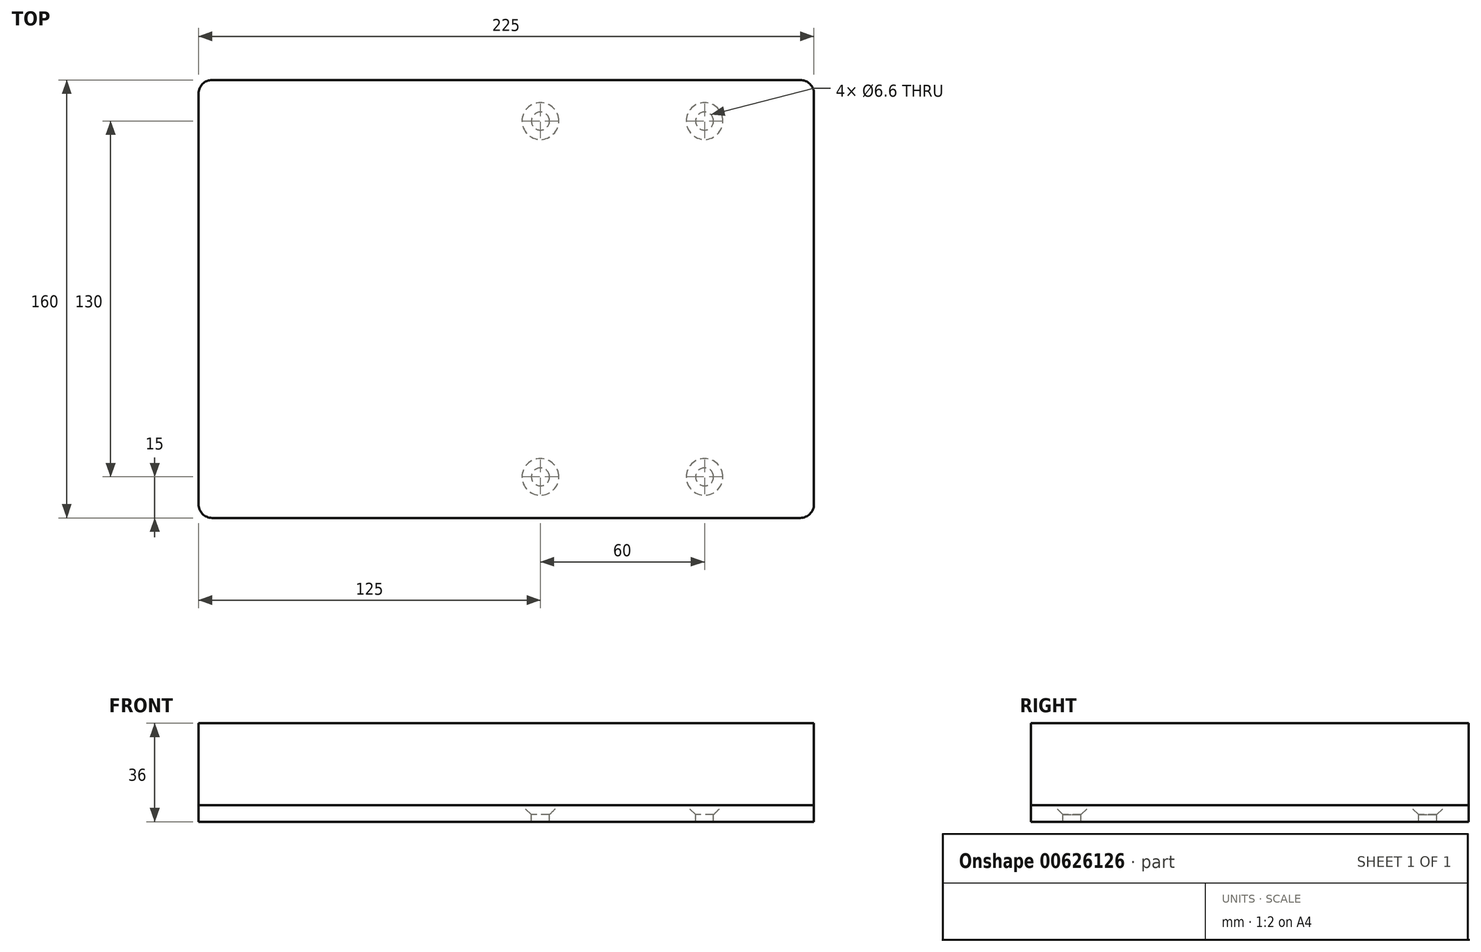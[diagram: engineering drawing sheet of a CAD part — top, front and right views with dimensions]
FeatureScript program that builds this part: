
annotation { "Feature Type Name" : "Feature", "Feature Type Description" : "" }
export const myFeature = defineFeature(function(context is Context, id is Id, definition is map)
    precondition{}
    {
        {
            var Q0;
            Q0=qCreatedBy(makeId("Top.planeOp"),FACE);
            var sketch = newSketch(context, id + "F0", { "sketchPlane" : qUnion([Q0])});
            skLineSegment(sketch, "E0.bottom", {"start": v(112.5, -80) * mm, "end": v(-112.5, -80) * mm});
            skLineSegment(sketch, "E0.top", {"start": v(112.5, 80) * mm, "end": v(-112.5, 80) * mm});
            skLineSegment(sketch, "E0.left", {"start": v(112.5, -80) * mm, "end": v(112.5, 80) * mm});
            skLineSegment(sketch, "E0.right", {"start": v(-112.5, -80) * mm, "end": v(-112.5, 80) * mm});
            skPoint(sketch, "E0.middle", {"position": v(0, 0) * mm});
            skSolve(sketch);
        }
        {
            var Q0;
            Q0=makeQuery(id+"F0.imprint","IMPRINT",FACE,{"disambiguationData":[TD([[makeQuery(id+"F0.imprint","IMPRINT",EDGE,{"derivedFrom":sQuery(id+"F0.wireOp",EDGE,"E0.bottom")}),-1.0]])]});
            extrude(context, id + "F1", {"entities" : qUnion([Q0]), "depth" : 6 * mm, "offsetDistance" : 25 * mm});
        }
        {
            var Q0;
            Q0=makeQuery(id+"F1.opExtrude","SWEPT_EDGE",EDGE,{"disambiguationData":[OSD([sQuery(id+"F0.wireOp",EDGE,"E0.bottom"),sQuery(id+"F0.wireOp",EDGE,"E0.left")])]});
            var Q1;
            Q1=makeQuery(id+"F1.opExtrude","SWEPT_EDGE",EDGE,{"disambiguationData":[OSD([sQuery(id+"F0.wireOp",EDGE,"E0.top"),sQuery(id+"F0.wireOp",EDGE,"E0.left")])]});
            var Q2;
            Q2=makeQuery(id+"F1.opExtrude","SWEPT_EDGE",EDGE,{"disambiguationData":[OSD([sQuery(id+"F0.wireOp",EDGE,"E0.bottom"),sQuery(id+"F0.wireOp",EDGE,"E0.right")])]});
            var Q3;
            Q3=makeQuery(id+"F1.opExtrude","SWEPT_EDGE",EDGE,{"disambiguationData":[OSD([sQuery(id+"F0.wireOp",EDGE,"E0.top"),sQuery(id+"F0.wireOp",EDGE,"E0.right")])]});
            fillet(context, id + "F2", {"entities" : qUnion([Q0, Q1, Q2, Q3]), "radius" : 5 * mm, "tangentPropagation" : true, "allowEdgeOverflow" : false});
        }
        {
            var Q0;
            Q0=makeQuery(id+"F1.opExtrude","CAP_FACE",FACE,{"disambiguationData":[OSD([sQuery(id+"F0.wireOp",EDGE,"E0.bottom"),sQuery(id+"F0.wireOp",EDGE,"E0.top"),sQuery(id+"F0.wireOp",EDGE,"E0.left"),sQuery(id+"F0.wireOp",EDGE,"E0.right")])],"isStart":false});
            var sketch = newSketch(context, id + "F3", { "sketchPlane" : qUnion([Q0])});
            skLineSegment(sketch, "E1", {"start": v(-230.2, 65) * mm, "end": v(230.97, 65) * mm, "construction": true});
            skLineSegment(sketch, "E2.MirrorCS", {"start": v(-230.2, -65) * mm, "end": v(230.97, -65) * mm, "construction": true});
            skLineSegment(sketch, "E3", {"start": v(72.5, 103.35) * mm, "end": v(72.5, -117.14) * mm, "construction": true});
            skLineSegment(sketch, "E4", {"start": v(12.5, 112.23) * mm, "end": v(12.5, -117.14) * mm, "construction": true});
            skPoint(sketch, "E5", {"position": v(12.5, 65) * mm});
            skPoint(sketch, "E6", {"position": v(72.5, 65) * mm});
            skPoint(sketch, "E7", {"position": v(12.5, -65) * mm});
            skPoint(sketch, "E8", {"position": v(72.5, -65) * mm});
            skSolve(sketch);
        }
        {
            var Q0;
            Q0=sQuery(id+"F3.wireOp",VERTEX,"E7");
            var Q1;
            Q1=sQuery(id+"F3.wireOp",VERTEX,"E8");
            var Q2;
            Q2=sQuery(id+"F3.wireOp",VERTEX,"E6");
            var Q3;
            Q3=sQuery(id+"F3.wireOp",VERTEX,"E5");
            var Q4;
            Q4=makeQuery(id+"F1.opExtrude","SWEPT_BODY",BODY,{"disambiguationData":[OSD([sQuery(id+"F0.wireOp",EDGE,"E0.bottom"),sQuery(id+"F0.wireOp",EDGE,"E0.top"),sQuery(id+"F0.wireOp",EDGE,"E0.left"),sQuery(id+"F0.wireOp",EDGE,"E0.right")])]});
            hole(context, id + "F4", {"style" : HoleStyle.C_SINK, "endStyle" : HoleEndStyle.BLIND, "standardTappedOrClearance" : lookupTablePath({ "standard" : "ISO", "fit" : "Normal", "size" : "M6", "type" : "Clearance" }), "standardBlindInLast" : lookupTablePath({ "fit" : "Standard", "standard" : "ISO", "size" : "M6", "type" : "Clearance" }), "holeDiameter" : 6.6 * mm, "cSinkDiameter" : 13.44 * mm, "cSinkAngle" : 90 * degree, "majorDiameter" : 5 * mm, "holeDepth" : 7 * mm, "isTappedThrough" : true, "tappedDepth" : 8 * mm, "tapClearance" : 3, "locations" : qUnion([Q0, Q1, Q2, Q3]), "scope" : qUnion([Q4])});
        }
        {
            var Q0;
            Q0=makeQuery(id+"F1.opExtrude","CAP_FACE",FACE,{"disambiguationData":[OSD([sQuery(id+"F0.wireOp",EDGE,"E0.bottom"),sQuery(id+"F0.wireOp",EDGE,"E0.top"),sQuery(id+"F0.wireOp",EDGE,"E0.left"),sQuery(id+"F0.wireOp",EDGE,"E0.right")])],"isStart":false});
            var sketch = newSketch(context, id + "F5", { "sketchPlane" : qUnion([Q0])});
            skLineSegment(sketch, "E9.0.0", {"start": v(112.5, -75) * mm, "end": v(112.5, 75) * mm});
            skArc(sketch, "E9.0.1", {"start": v(112.5, 75) * mm, "mid": v(111.04, 78.54) * mm, "end": v(107.5, 80) * mm});
            skLineSegment(sketch, "E9.0.2", {"start": v(107.5, 80) * mm, "end": v(-107.5, 80) * mm});
            skArc(sketch, "E9.0.3", {"start": v(-107.5, 80) * mm, "mid": v(-111.04, 78.54) * mm, "end": v(-112.5, 75) * mm});
            skLineSegment(sketch, "E9.0.4", {"start": v(-112.5, 75) * mm, "end": v(-112.5, -75) * mm});
            skArc(sketch, "E9.0.5", {"start": v(-112.5, -75) * mm, "mid": v(-111.04, -78.54) * mm, "end": v(-107.5, -80) * mm});
            skLineSegment(sketch, "E9.0.6", {"start": v(-107.5, -80) * mm, "end": v(107.5, -80) * mm});
            skArc(sketch, "E9.0.7", {"start": v(107.5, -80) * mm, "mid": v(111.04, -78.54) * mm, "end": v(112.5, -75) * mm});
            skSolve(sketch);
        }
        {
            var Q0;
            Q0 = qSketchRegion(id + "F5", true);
            extrude(context, id + "F6", {"entities" : qUnion([Q0]), "depth" : 30 * mm, "offsetDistance" : 25 * mm});
        }
    });
